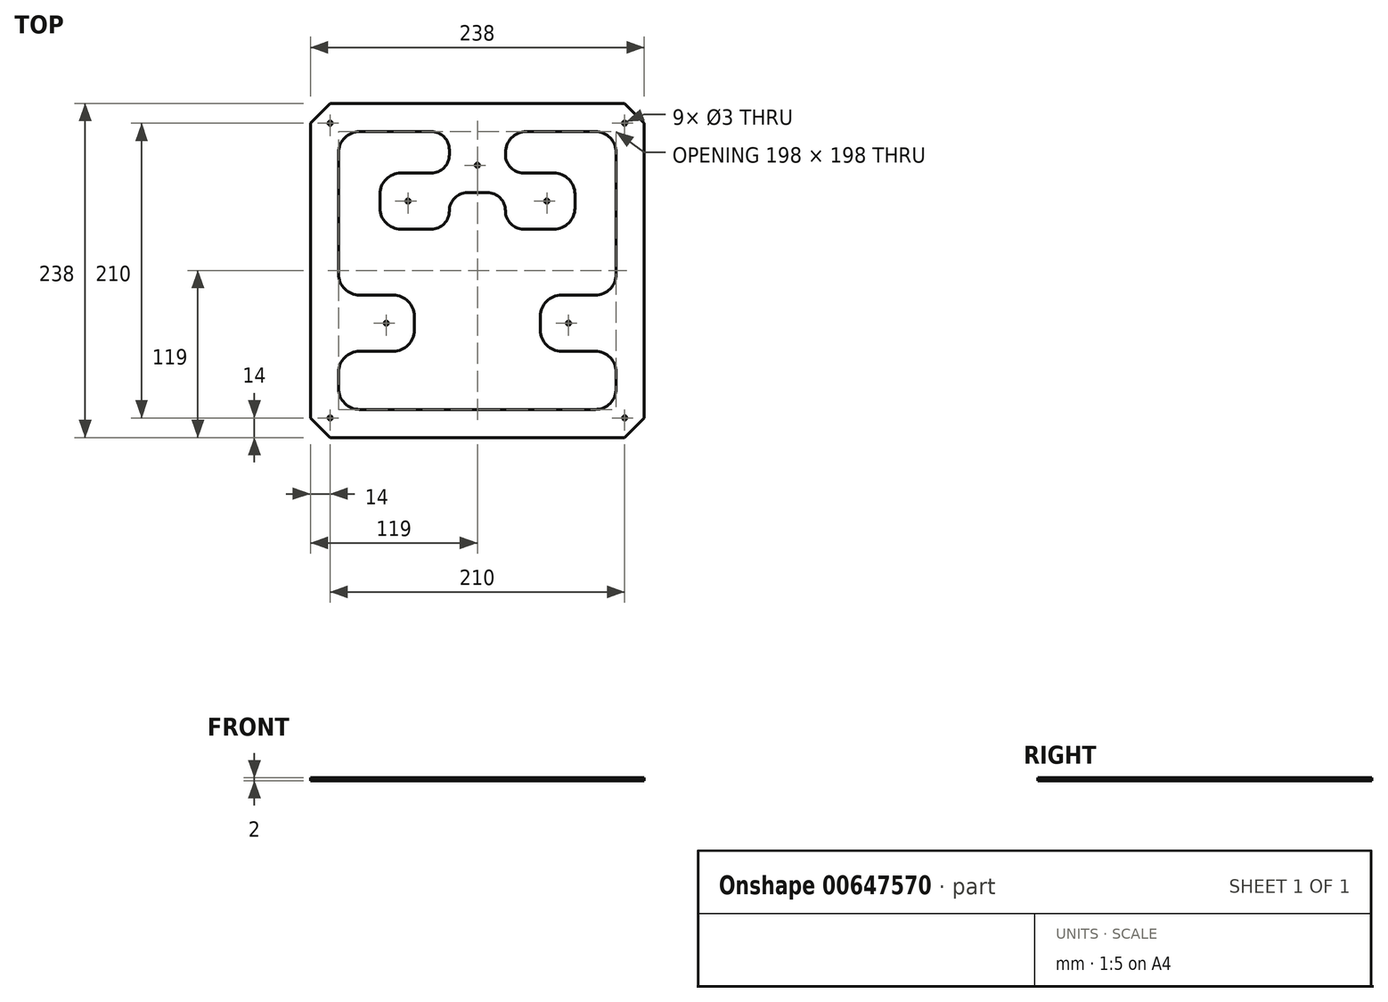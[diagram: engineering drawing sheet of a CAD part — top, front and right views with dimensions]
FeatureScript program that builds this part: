
annotation { "Feature Type Name" : "Feature", "Feature Type Description" : "" }
export const myFeature = defineFeature(function(context is Context, id is Id, definition is map)
    precondition{}
    {
        {
            var Q0;
            Q0=qCreatedBy(makeId("Top.planeOp"),FACE);
            var sketch = newSketch(context, id + "F0", { "sketchPlane" : qUnion([Q0])});
            skLineSegment(sketch, "E0.bottom", {"start": v(105, 119) * mm, "end": v(-105, 119) * mm});
            skLineSegment(sketch, "E0.top", {"start": v(105, -119) * mm, "end": v(-105, -119) * mm});
            skLineSegment(sketch, "E0.left", {"start": v(119, 105) * mm, "end": v(119, -105) * mm});
            skLineSegment(sketch, "E0.right", {"start": v(-119, 105) * mm, "end": v(-119, -105) * mm});
            skPoint(sketch, "E0.middle", {"position": v(0, 0) * mm});
            skLineSegment(sketch, "E1.bottom", {"start": v(105, 105) * mm, "end": v(-105, 105) * mm, "construction": true});
            skLineSegment(sketch, "E1.top", {"start": v(105, -105) * mm, "end": v(-105, -105) * mm, "construction": true});
            skLineSegment(sketch, "E1.left", {"start": v(105, 105) * mm, "end": v(105, -105) * mm, "construction": true});
            skLineSegment(sketch, "E1.right", {"start": v(-105, 105) * mm, "end": v(-105, -105) * mm, "construction": true});
            skPoint(sketch, "E2", {"position": v(-105, 105) * mm});
            skPoint(sketch, "E3", {"position": v(105, 105) * mm});
            skPoint(sketch, "E4", {"position": v(105, -105) * mm});
            skPoint(sketch, "E5", {"position": v(-105, -105) * mm});
            skLineSegment(sketch, "E6", {"start": v(-119, 105) * mm, "end": v(-105, 119) * mm});
            skPoint(sketch, "E7.orphan", {"position": v(-119, 119) * mm});
            skLineSegment(sketch, "E8", {"start": v(105, 119) * mm, "end": v(119, 105) * mm});
            skPoint(sketch, "E9.orphan", {"position": v(119, 119) * mm});
            skLineSegment(sketch, "E10", {"start": v(-119, -105) * mm, "end": v(-105, -119) * mm});
            skPoint(sketch, "E11.orphan", {"position": v(-119, -119) * mm});
            skLineSegment(sketch, "E12", {"start": v(105, -119) * mm, "end": v(119, -105) * mm});
            skPoint(sketch, "E13.orphan", {"position": v(119, -119) * mm});
            skLineSegment(sketch, "E14", {"start": v(0, 119) * mm, "end": v(0, -119) * mm, "construction": true});
            skCircle(sketch, "E15", {"center": v(0, 0) * mm, "radius": 75 * mm, "construction": true});
            skPoint(sketch, "E16", {"position": v(0, 75) * mm});
            skLineSegment(sketch, "E17", {"start": v(-119, 0) * mm, "end": v(119, 0) * mm, "construction": true});
            skPoint(sketch, "E18.1.0", {"position": v(-64.95, -37.5) * mm});
            skPoint(sketch, "E18.2.0", {"position": v(64.95, -37.5) * mm});
            skLineSegment(sketch, "E19", {"start": v(-49.5, 49.5) * mm, "end": v(49.5, 49.5) * mm, "construction": true});
            skPoint(sketch, "E20", {"position": v(0, 49.5) * mm});
            skSolve(sketch);
        }
        {
            var Q0;
            Q0=makeQuery(id+"F0.imprint","IMPRINT",FACE,{"disambiguationData":[TD([[makeQuery(id+"F0.imprint","IMPRINT",EDGE,{"derivedFrom":sQuery(id+"F0.wireOp",EDGE,"E0.bottom")}),1.0]])]});
            extrude(context, id + "F1", {"entities" : qUnion([Q0]), "depth" : 2 * mm, "offsetDistance" : 25 * mm});
        }
        {
            var Q0;
            Q0=sQuery(id+"F0.wireOp",VERTEX,"E2");
            var Q1;
            Q1=sQuery(id+"F0.wireOp",VERTEX,"E3");
            var Q2;
            Q2=sQuery(id+"F0.wireOp",VERTEX,"E5");
            var Q3;
            Q3=sQuery(id+"F0.wireOp",VERTEX,"E4");
            var Q4;
            Q4=sQuery(id+"F0.wireOp",VERTEX,"E16");
            var Q5;
            Q5=sQuery(id+"F0.wireOp",VERTEX,"E18.2.0");
            var Q6;
            Q6=sQuery(id+"F0.wireOp",VERTEX,"E18.1.0");
            var Q7;
            Q7=sQuery(id+"F0.wireOp",VERTEX,"E19.start");
            var Q8;
            Q8=sQuery(id+"F0.wireOp",VERTEX,"E19.end");
            var Q9;
            Q9=makeQuery(id+"F1.opExtrude","SWEPT_BODY",BODY,{"disambiguationData":[OSD([sQuery(id+"F0.wireOp",EDGE,"E0.bottom"),sQuery(id+"F0.wireOp",EDGE,"E0.top"),sQuery(id+"F0.wireOp",EDGE,"E0.left"),sQuery(id+"F0.wireOp",EDGE,"E0.right"),sQuery(id+"F0.wireOp",EDGE,"E6"),sQuery(id+"F0.wireOp",EDGE,"E8"),sQuery(id+"F0.wireOp",EDGE,"E10"),sQuery(id+"F0.wireOp",EDGE,"E12")])]});
            hole(context, id + "F2", {"style" : HoleStyle.SIMPLE, "endStyle" : HoleEndStyle.THROUGH, "oppositeDirection" : true, "holeDiameter" : 3 * mm, "majorDiameter" : 5 * mm, "isTappedThrough" : true, "tappedDepth" : 12 * mm, "tapClearance" : 3, "startFromSketch" : true, "locations" : qUnion([Q0, Q1, Q2, Q3, Q4, Q5, Q6, Q7, Q8]), "scope" : qUnion([Q9])});
        }
        {
            var Q0;
            Q0=makeQuery(id+"F1.opExtrude","CAP_FACE",FACE,{"disambiguationData":[OSD([sQuery(id+"F0.wireOp",EDGE,"E0.bottom"),sQuery(id+"F0.wireOp",EDGE,"E0.top"),sQuery(id+"F0.wireOp",EDGE,"E0.left"),sQuery(id+"F0.wireOp",EDGE,"E0.right"),sQuery(id+"F0.wireOp",EDGE,"E6"),sQuery(id+"F0.wireOp",EDGE,"E8"),sQuery(id+"F0.wireOp",EDGE,"E10"),sQuery(id+"F0.wireOp",EDGE,"E12")])],"isStart":false});
            var sketch = newSketch(context, id + "F3", { "sketchPlane" : qUnion([Q0])});
            skLineSegment(sketch, "E21", {"start": v(-99, -2.5) * mm, "end": v(-99, 84) * mm});
            skLineSegment(sketch, "E22", {"start": v(35, 99) * mm, "end": v(84, 99) * mm});
            skLineSegment(sketch, "E23", {"start": v(99, 84) * mm, "end": v(99, 40.75) * mm});
            skLineSegment(sketch, "E24", {"start": v(84, -99) * mm, "end": v(-84, -99) * mm});
            skPoint(sketch, "E25.visualSharp", {"position": v(-99, 99) * mm});
            skArc(sketch, "E25.filletArc", {"start": v(-84, 99) * mm, "mid": v(-94.6, 94.6) * mm, "end": v(-99, 84) * mm});
            skPoint(sketch, "E26.visualSharp", {"position": v(99, 99) * mm});
            skArc(sketch, "E26.filletArc", {"start": v(99, 84) * mm, "mid": v(94.6, 94.6) * mm, "end": v(84, 99) * mm});
            skPoint(sketch, "E27.visualSharp", {"position": v(99, -99) * mm});
            skArc(sketch, "E27.filletArc", {"start": v(84, -99) * mm, "mid": v(94.6, -94.6) * mm, "end": v(99, -84) * mm});
            skPoint(sketch, "E28.visualSharp", {"position": v(-99, -99) * mm});
            skArc(sketch, "E28.filletArc", {"start": v(-99, -84) * mm, "mid": v(-94.6, -94.6) * mm, "end": v(-84, -99) * mm});
            skLineSegment(sketch, "E29", {"start": v(-64.95, -37.5) * mm, "end": v(-99, -37.5) * mm, "construction": true});
            skLineSegment(sketch, "E30", {"start": v(-64.95, -37.5) * mm, "end": v(-44.95, -37.5) * mm, "construction": true});
            skLineSegment(sketch, "E31", {"start": v(-44.95, -32.5) * mm, "end": v(-44.95, -42.5) * mm});
            skLineSegment(sketch, "E32", {"start": v(-59.95, -17.5) * mm, "end": v(-84, -17.5) * mm});
            skArc(sketch, "E33.filletArc", {"start": v(-99, -2.5) * mm, "mid": v(-94.6, -13.1) * mm, "end": v(-84, -17.5) * mm});
            skPoint(sketch, "E34.visualSharp", {"position": v(-44.95, -17.5) * mm});
            skArc(sketch, "E34.filletArc", {"start": v(-44.95, -32.5) * mm, "mid": v(-49.35, -21.9) * mm, "end": v(-59.95, -17.5) * mm});
            skLineSegment(sketch, "E35", {"start": v(-59.95, -57.5) * mm, "end": v(-84, -57.5) * mm});
            skPoint(sketch, "E36.visualSharp", {"position": v(-44.95, -57.5) * mm});
            skArc(sketch, "E36.filletArc", {"start": v(-59.95, -57.5) * mm, "mid": v(-49.35, -53.1) * mm, "end": v(-44.95, -42.5) * mm});
            skLineSegment(sketch, "E37", {"start": v(-99, -72.5) * mm, "end": v(-99, -84) * mm});
            skPoint(sketch, "E38.visualSharp", {"position": v(-99, -57.5) * mm});
            skArc(sketch, "E38.filletArc", {"start": v(-84, -57.5) * mm, "mid": v(-94.6, -61.9) * mm, "end": v(-99, -72.5) * mm});
            skLineSegment(sketch, "E39", {"start": v(0, 50.24) * mm, "end": v(0, 99) * mm, "construction": true});
            skPoint(sketch, "E39.endSnap0", {"position": v(0, 99) * mm});
            skPoint(sketch, "E40.orphan", {"position": v(0, 75) * mm});
            skLineSegment(sketch, "E41", {"start": v(-20, 82.5) * mm, "end": v(-20, 86) * mm});
            skLineSegment(sketch, "E42", {"start": v(20, 82.5) * mm, "end": v(20, 84) * mm});
            skArc(sketch, "E43.filletArc", {"start": v(35, 99) * mm, "mid": v(24.4, 94.6) * mm, "end": v(20, 84) * mm});
            skLineSegment(sketch, "E44", {"start": v(-33, 99) * mm, "end": v(-84, 99) * mm});
            skPoint(sketch, "E45.visualSharp", {"position": v(-20, 99) * mm});
            skLineSegment(sketch, "E46", {"start": v(44.95, -37.5) * mm, "end": v(99, -37.5) * mm, "construction": true});
            skPoint(sketch, "E47.orphan", {"position": v(64.95, -37.5) * mm});
            skLineSegment(sketch, "E48", {"start": v(44.95, -37.5) * mm, "end": v(44.95, -32.5) * mm});
            skLineSegment(sketch, "E49", {"start": v(59.95, -17.5) * mm, "end": v(84, -17.5) * mm});
            skLineSegment(sketch, "E50", {"start": v(44.95, -37.5) * mm, "end": v(44.95, -42.5) * mm});
            skLineSegment(sketch, "E51", {"start": v(59.95, -57.5) * mm, "end": v(84, -57.5) * mm});
            skArc(sketch, "E52.filletArc", {"start": v(84, -17.5) * mm, "mid": v(94.6, -13.1) * mm, "end": v(99, -2.5) * mm});
            skLineSegment(sketch, "E53", {"start": v(99, -72.5) * mm, "end": v(99, -84) * mm});
            skPoint(sketch, "E54.visualSharp", {"position": v(44.95, -17.5) * mm});
            skArc(sketch, "E54.filletArc", {"start": v(59.95, -17.5) * mm, "mid": v(49.35, -21.9) * mm, "end": v(44.95, -32.5) * mm});
            skPoint(sketch, "E55.visualSharp", {"position": v(44.95, -57.5) * mm});
            skArc(sketch, "E55.filletArc", {"start": v(44.95, -42.5) * mm, "mid": v(49.35, -53.1) * mm, "end": v(59.95, -57.5) * mm});
            skPoint(sketch, "E56.visualSharp", {"position": v(99, -57.5) * mm});
            skArc(sketch, "E56.filletArc", {"start": v(99, -72.5) * mm, "mid": v(94.6, -61.9) * mm, "end": v(84, -57.5) * mm});
            skCircle(sketch, "E57", {"center": v(0, 0) * mm, "radius": 12.5 * mm});
            skLineSegment(sketch, "E58", {"start": v(-119, 0) * mm, "end": v(119, 0) * mm, "construction": true});
            skLineSegment(sketch, "E59", {"start": v(127.52, 47.1) * mm, "end": v(127.52, -47.1) * mm, "construction": true});
            skPoint(sketch, "E60", {"position": v(127.52, 0) * mm});
            skPoint(sketch, "E61.startSnap0", {"position": v(99, 40.75) * mm});
            skLineSegment(sketch, "E62.trimOffspring", {"start": v(99, 40.75) * mm, "end": v(99, -2.5) * mm});
            skLineSegment(sketch, "E63.bottom", {"start": v(119, -47.1) * mm, "end": v(110, -47.1) * mm});
            skLineSegment(sketch, "E63.top", {"start": v(119, -48.9) * mm, "end": v(110, -48.9) * mm});
            skLineSegment(sketch, "E63.left", {"start": v(119, -47.1) * mm, "end": v(119, -48.9) * mm});
            skLineSegment(sketch, "E63.right", {"start": v(110, -47.1) * mm, "end": v(110, -48.9) * mm});
            skLineSegment(sketch, "E64.bottom", {"start": v(119, 48.9) * mm, "end": v(110, 48.9) * mm});
            skLineSegment(sketch, "E64.top", {"start": v(119, 47.1) * mm, "end": v(110, 47.1) * mm});
            skLineSegment(sketch, "E64.left", {"start": v(119, 48.9) * mm, "end": v(119, 47.1) * mm});
            skLineSegment(sketch, "E64.right", {"start": v(110, 48.9) * mm, "end": v(110, 47.1) * mm});
            skLineSegment(sketch, "E65", {"start": v(-33, 69.5) * mm, "end": v(-54.5, 69.5) * mm});
            skLineSegment(sketch, "E66", {"start": v(-69.5, 54.5) * mm, "end": v(-69.5, 44.5) * mm});
            skLineSegment(sketch, "E67", {"start": v(-54.5, 29.5) * mm, "end": v(-33, 29.5) * mm});
            skLineSegment(sketch, "E68", {"start": v(69.5, 44.5) * mm, "end": v(69.5, 54.5) * mm});
            skLineSegment(sketch, "E69", {"start": v(54.5, 69.5) * mm, "end": v(33, 69.5) * mm});
            skArc(sketch, "E70.filletArc", {"start": v(-20, 86) * mm, "mid": v(-23.8, 95.2) * mm, "end": v(-33, 99) * mm});
            skPoint(sketch, "E71", {"position": v(-69.5, 49.5) * mm});
            skCircle(sketch, "E72.0", {"center": v(-49.5, 49.5) * mm, "radius": 1.5 * mm});
            skCircle(sketch, "E73.0", {"center": v(49.5, 49.5) * mm, "radius": 1.5 * mm});
            skPoint(sketch, "E74.visualSharp", {"position": v(-69.5, 69.5) * mm});
            skArc(sketch, "E74.filletArc", {"start": v(-54.5, 69.5) * mm, "mid": v(-65.1, 65.1) * mm, "end": v(-69.5, 54.5) * mm});
            skPoint(sketch, "E75.visualSharp", {"position": v(-69.5, 29.5) * mm});
            skArc(sketch, "E75.filletArc", {"start": v(-69.5, 44.5) * mm, "mid": v(-65.1, 33.9) * mm, "end": v(-54.5, 29.5) * mm});
            skPoint(sketch, "E76.visualSharp", {"position": v(69.5, 29.5) * mm});
            skArc(sketch, "E76.filletArc", {"start": v(54.5, 29.5) * mm, "mid": v(65.1, 33.9) * mm, "end": v(69.5, 44.5) * mm});
            skPoint(sketch, "E77.visualSharp", {"position": v(69.5, 69.5) * mm});
            skArc(sketch, "E77.filletArc", {"start": v(69.5, 54.5) * mm, "mid": v(65.1, 65.1) * mm, "end": v(54.5, 69.5) * mm});
            skPoint(sketch, "E78.newPointA", {"position": v(20, 69.5) * mm});
            skPoint(sketch, "E78.newPointB", {"position": v(20, 70) * mm});
            skArc(sketch, "E78.filletArc", {"start": v(20, 82.5) * mm, "mid": v(23.8, 73.3) * mm, "end": v(33, 69.5) * mm});
            skPoint(sketch, "E79.visualSharp", {"position": v(-20, 69.5) * mm});
            skArc(sketch, "E79.filletArc", {"start": v(-33, 69.5) * mm, "mid": v(-23.8, 73.3) * mm, "end": v(-20, 82.5) * mm});
            skLineSegment(sketch, "E80", {"start": v(-20, 42.5) * mm, "end": v(-20, 42.5) * mm});
            skLineSegment(sketch, "E81", {"start": v(-7, 55.5) * mm, "end": v(7, 55.5) * mm});
            skLineSegment(sketch, "E82", {"start": v(20, 42.5) * mm, "end": v(20, 42.5) * mm});
            skLineSegment(sketch, "E83.trimOffspring", {"start": v(33, 29.5) * mm, "end": v(54.5, 29.5) * mm});
            skPoint(sketch, "E84.visualSharp", {"position": v(-20, 55.5) * mm});
            skArc(sketch, "E84.filletArc", {"start": v(-7, 55.5) * mm, "mid": v(-16.2, 51.7) * mm, "end": v(-20, 42.5) * mm});
            skPoint(sketch, "E85.visualSharp", {"position": v(-20, 29.5) * mm});
            skArc(sketch, "E85.filletArc", {"start": v(-33, 29.5) * mm, "mid": v(-23.8, 33.3) * mm, "end": v(-20, 42.5) * mm});
            skPoint(sketch, "E86.visualSharp", {"position": v(20, 55.5) * mm});
            skArc(sketch, "E86.filletArc", {"start": v(20, 42.5) * mm, "mid": v(16.2, 51.7) * mm, "end": v(7, 55.5) * mm});
            skPoint(sketch, "E87.visualSharp", {"position": v(20, 29.5) * mm});
            skArc(sketch, "E87.filletArc", {"start": v(20, 42.5) * mm, "mid": v(23.8, 33.3) * mm, "end": v(33, 29.5) * mm});
            skPoint(sketch, "E88", {"position": v(0, 55.5) * mm});
            skSolve(sketch);
        }
        {
            var Q0;
            Q0=makeQuery(id+"F3.imprint","IMPRINT",FACE,{"disambiguationData":[TD([[makeQuery(id+"F3.imprint","IMPRINT",EDGE,{"derivedFrom":sQuery(id+"F3.wireOp",EDGE,"E21")}),-1.0]])]});
            var Q1;
            Q1=makeQuery(id+"F3.imprint","IMPRINT",FACE,{"disambiguationData":[TD([[makeQuery(id+"F3.imprint","IMPRINT",EDGE,{"derivedFrom":sQuery(id+"F3.wireOp",EDGE,"E57")}),1.0]])]});
            extrude(context, id + "F4", {"entities" : qUnion([Q0, Q1]), "operationType" : NewBodyOperationType.REMOVE, "oppositeDirection" : true, "depth" : 25 * mm, "offsetDistance" : 25 * mm});
        }
    });
